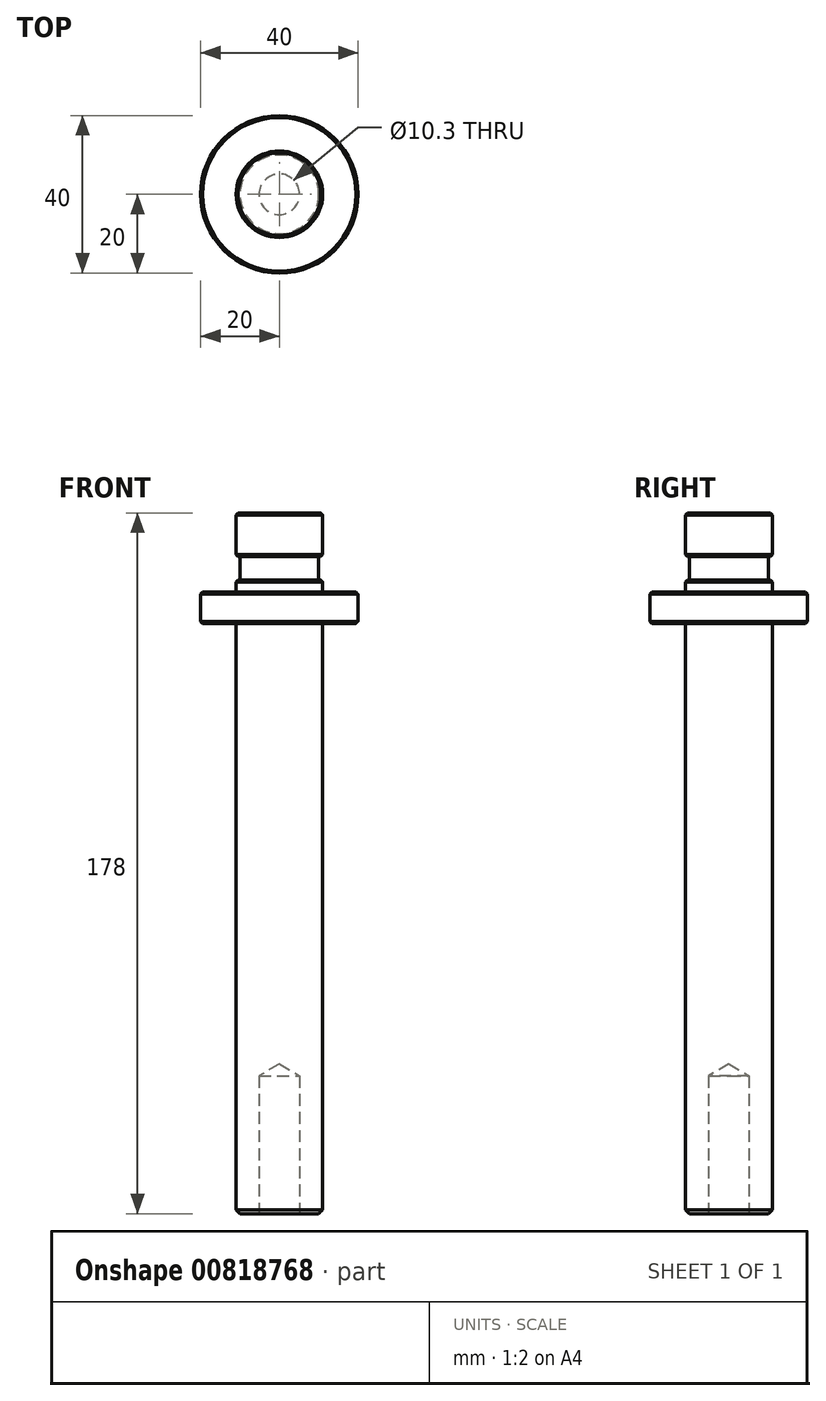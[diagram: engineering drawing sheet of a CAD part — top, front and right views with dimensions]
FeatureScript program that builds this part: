
annotation { "Feature Type Name" : "Feature", "Feature Type Description" : "" }
export const myFeature = defineFeature(function(context is Context, id is Id, definition is map)
    precondition{}
    {
        {
            var Q0;
            Q0=qCreatedBy(makeId("Top.planeOp"),FACE);
            var sketch = newSketch(context, id + "F0", { "sketchPlane" : qUnion([Q0])});
            skCircle(sketch, "E0", {"center": v(0, 0) * mm, "radius": 11 * mm});
            skSolve(sketch);
        }
        {
            var Q0;
            Q0 = qSketchRegion(id + "F0", true);
            extrude(context, id + "F1", {"entities" : qUnion([Q0]), "depth" : 150 * mm, "offsetDistance" : 25 * mm});
        }
        {
            var Q0;
            Q0=makeQuery(id+"F1.opExtrude","CAP_FACE",FACE,{"disambiguationData":[OSD([sQuery(id+"F0.wireOp",EDGE,"E0")])],"isStart":false});
            var sketch = newSketch(context, id + "F2", { "sketchPlane" : qUnion([Q0])});
            skCircle(sketch, "E1", {"center": v(0, 0) * mm, "radius": 20 * mm});
            skSolve(sketch);
        }
        {
            var Q0;
            Q0 = qSketchRegion(id + "F2", true);
            extrude(context, id + "F3", {"entities" : qUnion([Q0]), "operationType" : NewBodyOperationType.ADD, "depth" : 7.9 * mm, "offsetDistance" : 25 * mm});
        }
        {
            var Q0;
            Q0=makeQuery(id+"F3.opExtrude","CAP_FACE",FACE,{"disambiguationData":[OSD([sQuery(id+"F2.wireOp",EDGE,"E1")])],"isStart":false});
            var sketch = newSketch(context, id + "F4", { "sketchPlane" : qUnion([Q0])});
            skCircle(sketch, "E2", {"center": v(0, 0) * mm, "radius": 11 * mm});
            skSolve(sketch);
        }
        {
            var Q0;
            Q0 = qSketchRegion(id + "F4", true);
            extrude(context, id + "F5", {"entities" : qUnion([Q0]), "operationType" : NewBodyOperationType.ADD, "depth" : 3.1 * mm, "offsetDistance" : 25 * mm});
        }
        {
            var Q0;
            Q0=makeQuery(id+"F5.opExtrude","CAP_FACE",FACE,{"disambiguationData":[OSD([sQuery(id+"F4.wireOp",EDGE,"E2")])],"isStart":false});
            var sketch = newSketch(context, id + "F6", { "sketchPlane" : qUnion([Q0])});
            skCircle(sketch, "E3", {"center": v(0, 0) * mm, "radius": 10 * mm});
            skSolve(sketch);
        }
        {
            var Q0;
            Q0 = qSketchRegion(id + "F6", true);
            extrude(context, id + "F7", {"entities" : qUnion([Q0]), "operationType" : NewBodyOperationType.ADD, "depth" : 6 * mm, "offsetDistance" : 25 * mm});
        }
        {
            var Q0;
            Q0=makeQuery(id+"F7.opExtrude","CAP_FACE",FACE,{"disambiguationData":[OSD([sQuery(id+"F6.wireOp",EDGE,"E3")])],"isStart":false});
            var sketch = newSketch(context, id + "F8", { "sketchPlane" : qUnion([Q0])});
            skCircle(sketch, "E4", {"center": v(0, 0) * mm, "radius": 11 * mm});
            skSolve(sketch);
        }
        {
            var Q0;
            Q0 = qSketchRegion(id + "F8", true);
            extrude(context, id + "F9", {"entities" : qUnion([Q0]), "operationType" : NewBodyOperationType.ADD, "depth" : 11 * mm, "offsetDistance" : 25 * mm});
        }
        {
            var Q0;
            Q0=makeQuery(id+"F1.opExtrude","CAP_FACE",FACE,{"disambiguationData":[OSD([sQuery(id+"F0.wireOp",EDGE,"E0")])],"isStart":true});
            var sketch = newSketch(context, id + "F10", { "sketchPlane" : qUnion([Q0])});
            skPoint(sketch, "E5", {"position": v(0, 0) * mm});
            skSolve(sketch);
        }
        {
            var Q0;
            Q0=sQuery(id+"F10.wireOp",VERTEX,"E5");
            var Q1;
            Q1=makeQuery(id+"F1.opExtrude","SWEPT_BODY",BODY,{"disambiguationData":[OSD([sQuery(id+"F0.wireOp",EDGE,"E0")])]});
            hole(context, id + "F11", {"style" : HoleStyle.SIMPLE, "endStyle" : HoleEndStyle.BLIND, "standardTappedOrClearance" : lookupTablePath({ "standard" : "ISO", "engagement" : "75%", "pitch" : "1.75 mm", "size" : "M12", "type" : "Tapped" }), "standardBlindInLast" : lookupTablePath({ "standard" : "ISO", "engagement" : "75%", "pitch" : "1.75 mm", "size" : "M12", "type" : "Tapped" }), "holeDiameter" : 10.3 * mm, "majorDiameter" : 12 * mm, "showTappedDepth" : true, "holeDepth" : 35 * mm, "isTappedThrough" : true, "tappedDepth" : 29.75 * mm, "tapClearance" : 3, "startFromSketch" : true, "locations" : qUnion([Q0]), "scope" : qUnion([Q1])});
        }
        {
            var Q0;
            Q0=makeQuery(id+"F11.hole-0.boolean.opBoolean","COPY",EDGE,{"derivedFrom":makeQuery(id+"F11.hole-0.opRevolve","SWEPT_EDGE",EDGE,{"disambiguationData":[OSD([sQuery(id+"F11.hole-0.sketch.wireOp",EDGE,"core_line_2"),sQuery(id+"F11.hole-0.sketch.wireOp",EDGE,"core_line_3")])]})});
            var Q1;
            Q1=makeQuery(id+"F1.opExtrude","CAP_EDGE",EDGE,{"disambiguationData":[OSD([sQuery(id+"F0.wireOp",EDGE,"E0")])],"isStart":true});
            chamfer(context, id + "F12", {"entities" : qUnion([Q0, Q1]), "width" : 1 * mm, "tangentPropagation" : true});
        }
        {
            var Q0;
            Q0=makeQuery(id+"F3.opExtrude","CAP_EDGE",EDGE,{"disambiguationData":[OSD([sQuery(id+"F2.wireOp",EDGE,"E1")])],"isStart":true});
            var Q1;
            Q1=makeQuery(id+"F3.opExtrude","CAP_EDGE",EDGE,{"disambiguationData":[OSD([sQuery(id+"F2.wireOp",EDGE,"E1")])],"isStart":false});
            var Q2;
            Q2=makeQuery(id+"F5.opExtrude","CAP_EDGE",EDGE,{"disambiguationData":[OSD([sQuery(id+"F4.wireOp",EDGE,"E2")])],"isStart":false});
            var Q3;
            Q3=makeQuery(id+"F9.opExtrude","CAP_EDGE",EDGE,{"disambiguationData":[OSD([sQuery(id+"F8.wireOp",EDGE,"E4")])],"isStart":true});
            var Q4;
            Q4=makeQuery(id+"F9.opExtrude","CAP_EDGE",EDGE,{"disambiguationData":[OSD([sQuery(id+"F8.wireOp",EDGE,"E4")])],"isStart":false});
            chamfer(context, id + "F13", {"entities" : qUnion([Q0, Q1, Q2, Q3, Q4]), "width" : .5 * mm, "tangentPropagation" : true});
        }
    });
